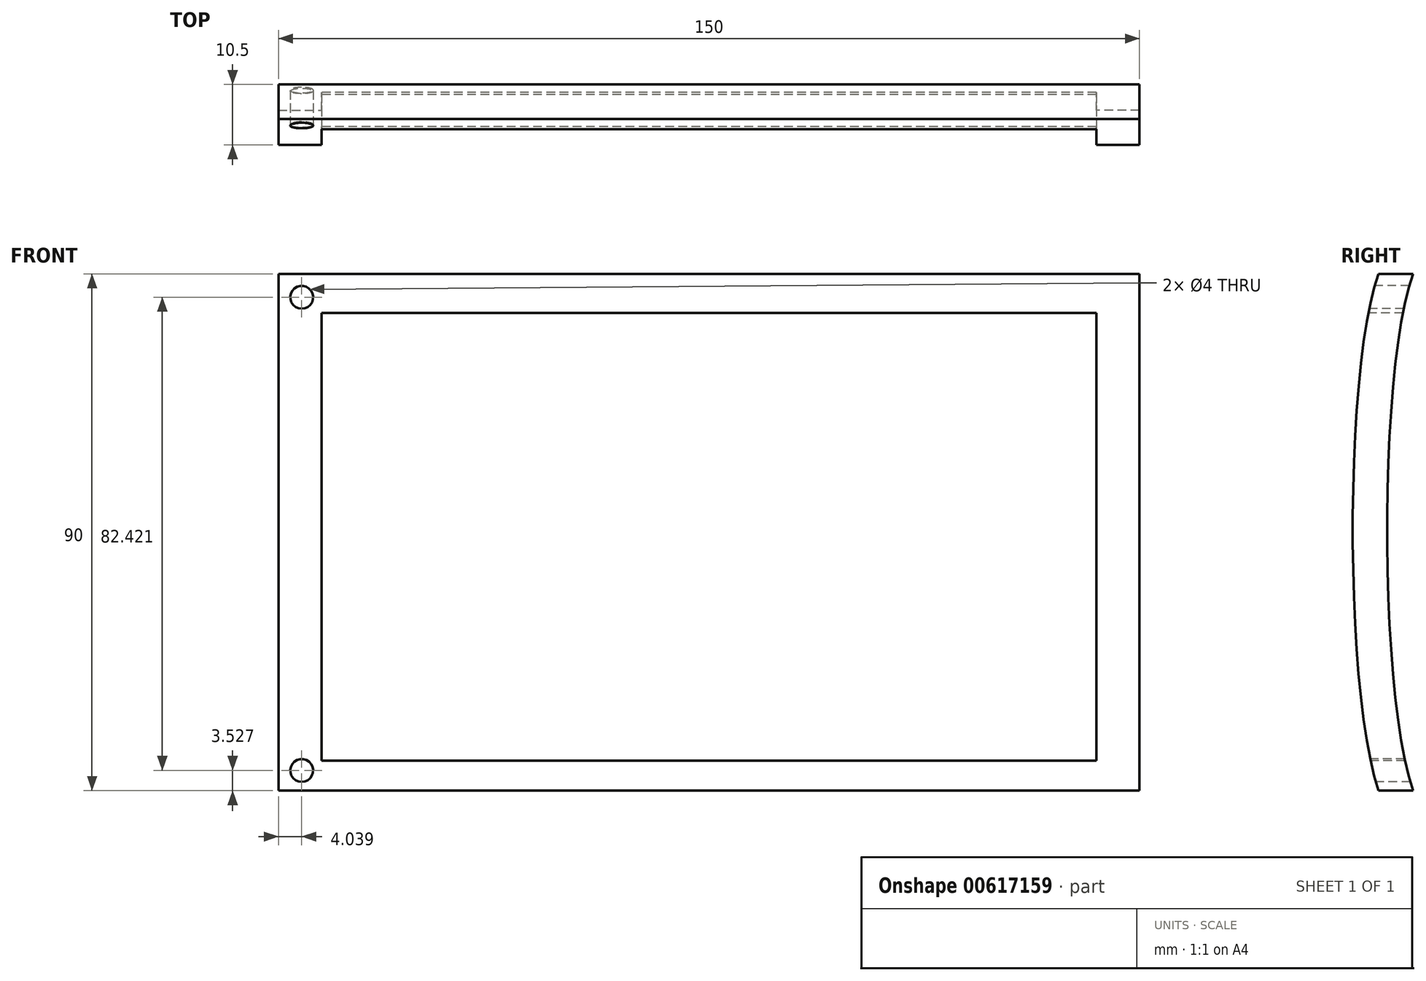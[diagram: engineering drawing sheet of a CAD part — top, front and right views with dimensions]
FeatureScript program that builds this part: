
annotation { "Feature Type Name" : "Feature", "Feature Type Description" : "" }
export const myFeature = defineFeature(function(context is Context, id is Id, definition is map)
    precondition{}
    {
        {
            var Q0;
            Q0=qCreatedBy(makeId("Right.planeOp"),FACE);
            var sketch = newSketch(context, id + "F0", { "sketchPlane" : qUnion([Q0])});
            skFitSpline(sketch, "E0", {"points": [v(0, 90) * mm, v(0, 0) * mm], "startDerivative": vector(-17.96, -49.78) * mm, "endDerivative": vector(18, -54) * mm});
            skLineSegment(sketch, "E1", {"start": v(0, 90) * mm, "end": v(6, 90) * mm});
            skLineSegment(sketch, "E2", {"start": v(6, 0) * mm, "end": v(0, 0) * mm});
            skFitSpline(sketch, "E3", {"points": [v(6, 90) * mm, v(6, 0) * mm], "startDerivative": vector(-18, -50.91) * mm, "endDerivative": vector(18, -54) * mm});
            skSolve(sketch);
        }
        {
            var Q0;
            Q0=makeQuery(id+"F0.imprint","IMPRINT",FACE,{"disambiguationData":[TD([[makeQuery(id+"F0.imprint","IMPRINT",EDGE,{"derivedFrom":sQuery(id+"F0.wireOp",EDGE,"E0")}),1.0]])]});
            extrude(context, id + "F1", {"entities" : qUnion([Q0]), "depth" : 75 * mm, "offsetDistance" : 25 * mm});
        }
        {
            var Q0;
            Q0=makeQuery(id+"F1.opExtrude","CAP_FACE",FACE,{"disambiguationData":[OSD([sQuery(id+"F0.wireOp",EDGE,"E0"),sQuery(id+"F0.wireOp",EDGE,"E1"),sQuery(id+"F0.wireOp",EDGE,"E2"),sQuery(id+"F0.wireOp",EDGE,"E3")])],"isStart":true});
            extrude(context, id + "F2", {"entities" : qUnion([Q0]), "operationType" : NewBodyOperationType.ADD, "depth" : 75 * mm, "offsetDistance" : 25 * mm});
        }
        {
            var Q0;
            Q0=qCreatedBy(makeId("Front.planeOp"),FACE);
            cPlane(context, id + "F3", {"entities" : qUnion([Q0]), "cplaneType" : CPlaneType.OFFSET, "offset" : 6 * mm, "width" : 150 * mm, "height" : 150 * mm});
        }
        {
            var Q0;
            Q0=qCreatedBy(id+"F3.planeOp",FACE);
            var sketch = newSketch(context, id + "F4", { "sketchPlane" : qUnion([Q0])});
            skLineSegment(sketch, "E4.bottom", {"start": v(-67.51, 83.23) * mm, "end": v(67.49, 83.23) * mm});
            skLineSegment(sketch, "E4.top", {"start": v(-67.51, 5.23) * mm, "end": v(67.49, 5.23) * mm});
            skLineSegment(sketch, "E4.left", {"start": v(-67.51, 83.23) * mm, "end": v(-67.51, 5.23) * mm});
            skLineSegment(sketch, "E4.right", {"start": v(67.49, 83.23) * mm, "end": v(67.49, 5.23) * mm});
            skSolve(sketch);
        }
        {
            var Q0;
            Q0=makeQuery(id+"F4.imprint","IMPRINT",FACE,{"disambiguationData":[TD([[makeQuery(id+"F4.imprint","IMPRINT",EDGE,{"derivedFrom":sQuery(id+"F4.wireOp",EDGE,"E4.bottom")}),-1.0]])]});
            extrude(context, id + "F5", {"entities" : qUnion([Q0]), "operationType" : NewBodyOperationType.REMOVE, "oppositeDirection" : true, "depth" : 12 * mm, "offsetDistance" : 25 * mm});
        }
        {
            var Q0;
            Q0=qCreatedBy(id+"F3.planeOp",FACE);
            var sketch = newSketch(context, id + "F6", { "sketchPlane" : qUnion([Q0])});
            skCircle(sketch, "E5", {"center": v(-70.96, 85.95) * mm, "radius": 2 * mm});
            skCircle(sketch, "E6", {"center": v(-70.96, 3.53) * mm, "radius": 2 * mm});
            skCircle(sketch, "E7.MirrorC", {"center": v(70.96, 85.95) * mm, "radius": 2 * mm});
            skCircle(sketch, "E8.MirrorC", {"center": v(70.96, 3.53) * mm, "radius": 2 * mm});
            skSolve(sketch);
        }
        {
            var Q0;
            Q0=makeQuery(id+"F6.imprint","IMPRINT",FACE,{"disambiguationData":[TD([[makeQuery(id+"F6.imprint","IMPRINT",EDGE,{"derivedFrom":sQuery(id+"F6.wireOp",EDGE,"E5")}),1.0]])]});
            var Q1;
            Q1=makeQuery(id+"F6.imprint","IMPRINT",FACE,{"disambiguationData":[TD([[makeQuery(id+"F6.imprint","IMPRINT",EDGE,{"derivedFrom":sQuery(id+"F6.wireOp",EDGE,"E7.MirrorC")}),-1.0]])]});
            var Q2;
            Q2=makeQuery(id+"F6.imprint","IMPRINT",FACE,{"disambiguationData":[TD([[makeQuery(id+"F6.imprint","IMPRINT",EDGE,{"derivedFrom":sQuery(id+"F6.wireOp",EDGE,"E8.MirrorC")}),-1.0]])]});
            var Q3;
            Q3=makeQuery(id+"F6.imprint","IMPRINT",FACE,{"disambiguationData":[TD([[makeQuery(id+"F6.imprint","IMPRINT",EDGE,{"derivedFrom":sQuery(id+"F6.wireOp",EDGE,"E6")}),1.0]])]});
            var Q4;
            Q4=sQuery(id+"F6.wireOp",EDGE,"E5");
            var Q5;
            Q5=sQuery(id+"F6.wireOp",EDGE,"E7.MirrorC");
            var Q6;
            Q6=sQuery(id+"F6.wireOp",EDGE,"E8.MirrorC");
            var Q7;
            Q7=sQuery(id+"F6.wireOp",EDGE,"E6");
            extrude(context, id + "F7", {"entities" : qUnion([Q0, Q1, Q2, Q3]), "operationType" : NewBodyOperationType.REMOVE, "surfaceEntities" : qUnion([Q4, Q5, Q6, Q7]), "oppositeDirection" : true, "depth" : 25 * mm, "offsetDistance" : 25 * mm});
        }
    });
